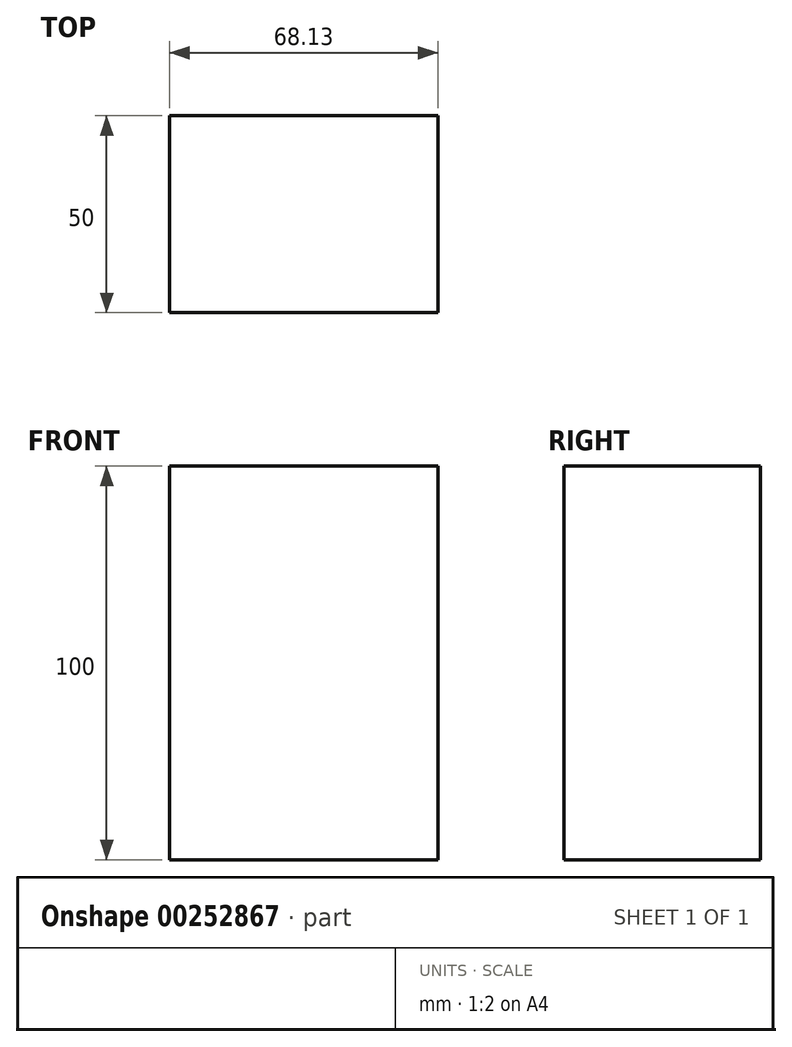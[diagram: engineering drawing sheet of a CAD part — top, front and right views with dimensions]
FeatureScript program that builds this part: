
annotation { "Feature Type Name" : "Feature", "Feature Type Description" : "" }
export const myFeature = defineFeature(function(context is Context, id is Id, definition is map)
    precondition{}
    {
        {
            var Q0;
            Q0=qCreatedBy(makeId("Front.planeOp"),FACE);
            var sketch = newSketch(context, id + "F0", { "sketchPlane" : qUnion([Q0])});
            skLineSegment(sketch, "E0.bottom", {"start": v(0, 0) * mm, "end": v(68.13, 0) * mm});
            skLineSegment(sketch, "E0.top", {"start": v(0, 50) * mm, "end": v(68.13, 50) * mm});
            skLineSegment(sketch, "E0.left", {"start": v(0, 0) * mm, "end": v(0, 50) * mm});
            skLineSegment(sketch, "E0.right", {"start": v(68.13, 0) * mm, "end": v(68.13, 50) * mm});
            skSolve(sketch);
        }
        {
            var Q0;
            Q0 = qSketchRegion(id + "F0", true);
            extrude(context, id + "F1", {"entities" : qUnion([Q0]), "depth" : 50 * mm});
        }
        {
            var Q0;
            Q0=makeQuery(id+"F1.opExtrude","SWEPT_BODY",BODY,{"disambiguationData":[OSD([sQuery(id+"F0.wireOp",EDGE,"E0.bottom"),sQuery(id+"F0.wireOp",EDGE,"E0.top"),sQuery(id+"F0.wireOp",EDGE,"E0.left"),sQuery(id+"F0.wireOp",EDGE,"E0.right")])]});
            var Q1;
            Q1=qCreatedBy(makeId("Top.planeOp"),FACE);
            mirror(context, id + "F2", {"operationType" : NewBodyOperationType.ADD, "entities" : qUnion([Q0]), "mirrorPlane" : qUnion([Q1])});
        }
    });
